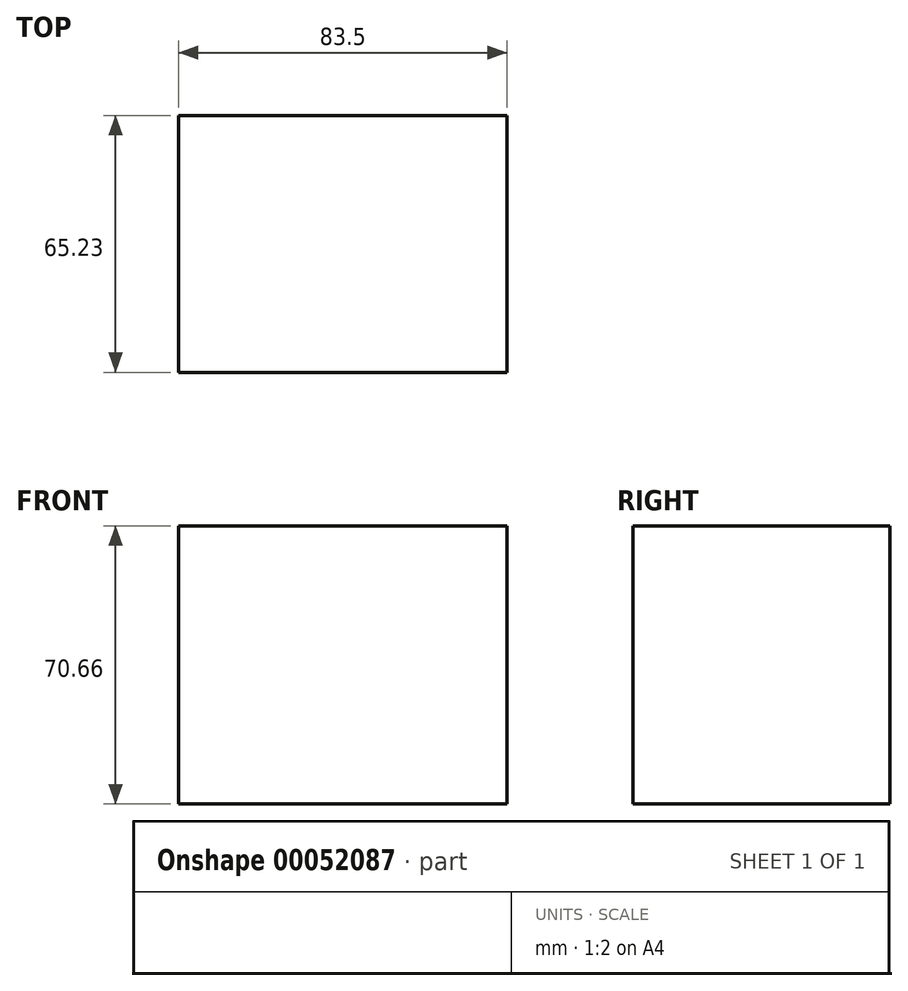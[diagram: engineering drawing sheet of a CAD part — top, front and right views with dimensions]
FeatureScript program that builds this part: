
annotation { "Feature Type Name" : "Feature", "Feature Type Description" : "" }
export const myFeature = defineFeature(function(context is Context, id is Id, definition is map)
    precondition{}
    {
        {
            var Q0;
            Q0=qCreatedBy(makeId("Top.planeOp"),FACE);
            var sketch = newSketch(context, id + "F0", { "sketchPlane" : qUnion([Q0])});
            skLineSegment(sketch, "E0.bottom", {"start": v(-48.69, -18.24) * mm, "end": v(34.81, -18.24) * mm});
            skLineSegment(sketch, "E0.top", {"start": v(-48.69, 46.99) * mm, "end": v(34.81, 46.99) * mm});
            skLineSegment(sketch, "E0.left", {"start": v(-48.69, -18.24) * mm, "end": v(-48.69, 46.99) * mm});
            skLineSegment(sketch, "E0.right", {"start": v(34.81, -18.24) * mm, "end": v(34.81, 46.99) * mm});
            skSolve(sketch);
        }
        {
            var Q0;
            Q0=makeQuery(id+"F0.imprint","IMPRINT",FACE,{"disambiguationData":[TD([[makeQuery(id+"F0.imprint","IMPRINT",EDGE,{"derivedFrom":sQuery(id+"F0.wireOp",EDGE,"E0.bottom")}),1.0]])]});
            extrude(context, id + "F1", {"entities" : qUnion([Q0]), "depth" : 70.66 * mm});
        }
    });
